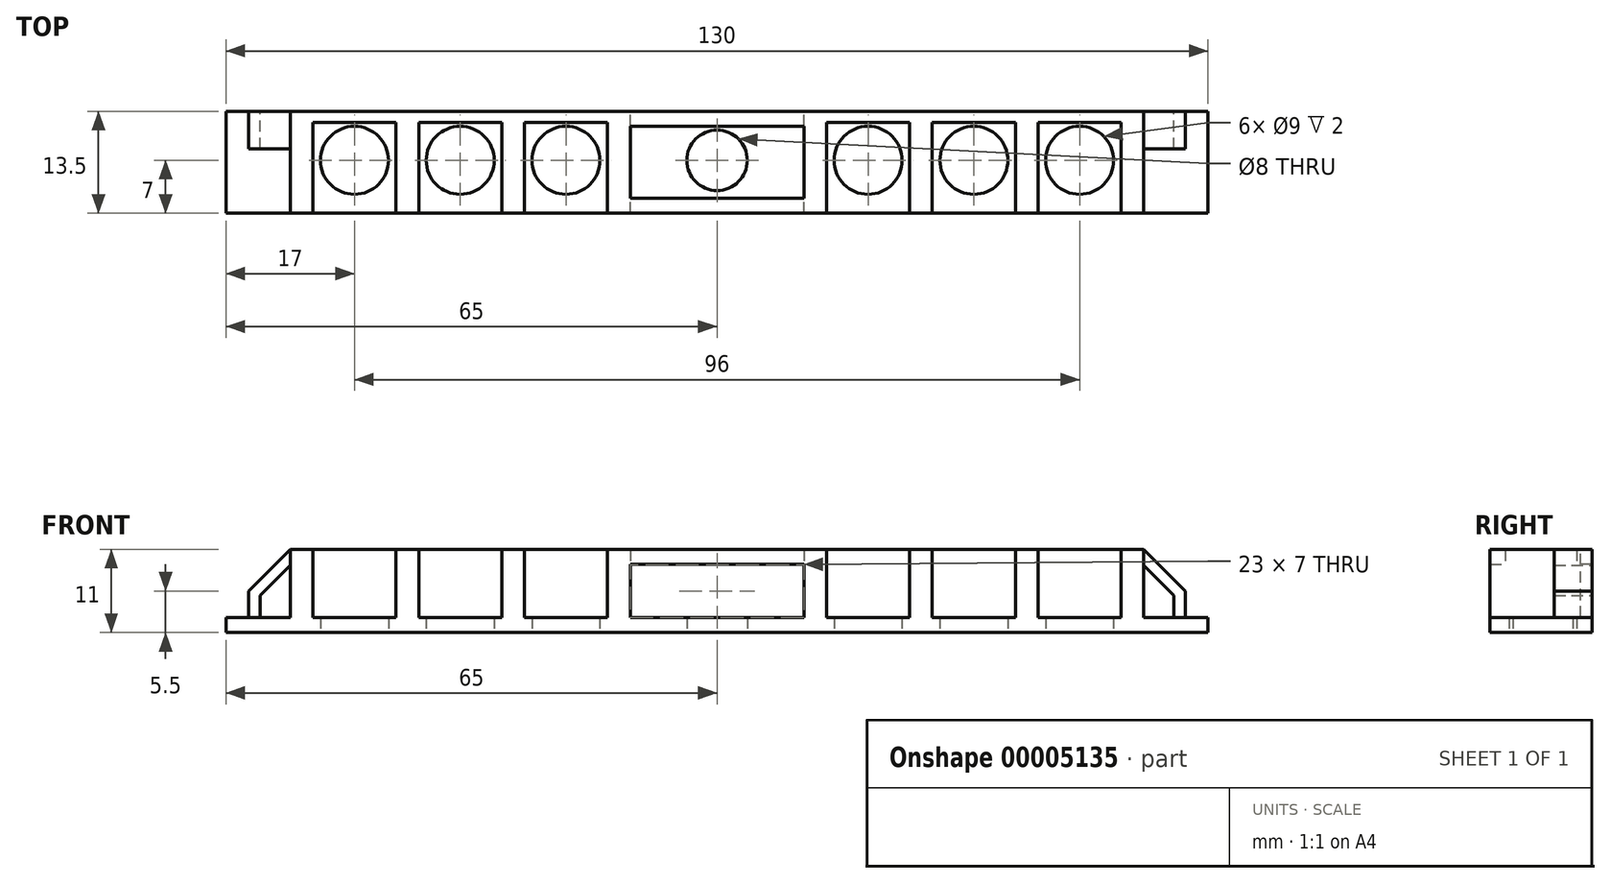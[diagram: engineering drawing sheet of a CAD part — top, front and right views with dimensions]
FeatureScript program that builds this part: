
annotation { "Feature Type Name" : "Feature", "Feature Type Description" : "" }
export const myFeature = defineFeature(function(context is Context, id is Id, definition is map)
    precondition{}
    {
        {
            var Q0;
            Q0=qCreatedBy(makeId("Top.planeOp"),FACE);
            var sketch = newSketch(context, id + "F0", { "sketchPlane" : qUnion([Q0])});
            skLineSegment(sketch, "E0", {"start": v(-20, 0) * mm, "end": v(-34, 0) * mm, "construction": true});
            skLineSegment(sketch, "E1", {"start": v(-34, 0) * mm, "end": v(-48, 0) * mm, "construction": true});
            skCircle(sketch, "E2", {"center": v(-20, 0) * mm, "radius": 4.5 * mm});
            skCircle(sketch, "E3", {"center": v(-34, 0) * mm, "radius": 4.5 * mm});
            skCircle(sketch, "E4", {"center": v(-48, 0) * mm, "radius": 4.5 * mm});
            skPoint(sketch, "E5", {"position": v(0, 0) * mm});
            skLineSegment(sketch, "E6.bottom", {"start": v(0, 6.5) * mm, "end": v(-65, 6.5) * mm});
            skLineSegment(sketch, "E6.top", {"start": v(0, -7) * mm, "end": v(-65, -7) * mm});
            skLineSegment(sketch, "E6.left", {"start": v(0, 6.5) * mm, "end": v(0, 4) * mm});
            skLineSegment(sketch, "E6.right", {"start": v(-65, 6.5) * mm, "end": v(-65, -7) * mm});
            skLineSegment(sketch, "E7", {"start": v(-20, 0) * mm, "end": v(-20, 6.5) * mm, "construction": true});
            skArc(sketch, "E8", {"start": v(0, 4) * mm, "mid": v(-4, 0) * mm, "end": v(0, -4) * mm});
            skLineSegment(sketch, "E9.trimOffspring", {"start": v(0, -4) * mm, "end": v(0, -7) * mm});
            skLineSegment(sketch, "E10", {"start": v(0, 4) * mm, "end": v(0, -4) * mm, "construction": true});
            skLineSegment(sketch, "E11", {"start": v(-20, 0) * mm, "end": v(0, 0) * mm, "construction": true});
            skSolve(sketch);
        }
        {
            var Q0;
            Q0 = qSketchRegion(id + "F0", true);
            extrude(context, id + "F1", {"entities" : qUnion([Q0]), "depth" : 2 * mm});
        }
        {
            var Q0;
            Q0=makeQuery(id+"F1.opExtrude","SWEPT_FACE",FACE,{"disambiguationData":[OSD([sQuery(id+"F0.wireOp",EDGE,"E6.bottom")])]});
            var sketch = newSketch(context, id + "F2", { "sketchPlane" : qUnion([Q0])});
            skLineSegment(sketch, "E12", {"start": v(20, 11) * mm, "end": v(20, 0) * mm, "construction": true});
            skLineSegment(sketch, "E13.bottom", {"start": v(11.5, 2) * mm, "end": v(14.5, 2) * mm});
            skLineSegment(sketch, "E13.top", {"start": v(11.5, 11) * mm, "end": v(14.5, 11) * mm});
            skLineSegment(sketch, "E13.left", {"start": v(11.5, 2) * mm, "end": v(11.5, 11) * mm});
            skLineSegment(sketch, "E13.right", {"start": v(14.5, 2) * mm, "end": v(14.5, 11) * mm});
            skLineSegment(sketch, "E14.bottom", {"start": v(25.5, 2) * mm, "end": v(28.5, 2) * mm});
            skLineSegment(sketch, "E14.top", {"start": v(25.5, 11) * mm, "end": v(28.5, 11) * mm});
            skLineSegment(sketch, "E14.left", {"start": v(25.5, 2) * mm, "end": v(25.5, 11) * mm});
            skLineSegment(sketch, "E14.right", {"start": v(28.5, 2) * mm, "end": v(28.5, 11) * mm});
            skLineSegment(sketch, "E15.bottom", {"start": v(39.5, 2) * mm, "end": v(42.5, 2) * mm});
            skLineSegment(sketch, "E15.top", {"start": v(39.5, 11) * mm, "end": v(42.5, 11) * mm});
            skLineSegment(sketch, "E15.left", {"start": v(39.5, 2) * mm, "end": v(39.5, 11) * mm});
            skLineSegment(sketch, "E15.right", {"start": v(42.5, 2) * mm, "end": v(42.5, 11) * mm});
            skLineSegment(sketch, "E16.bottom", {"start": v(53.5, 2) * mm, "end": v(56.5, 2) * mm});
            skLineSegment(sketch, "E16.top", {"start": v(53.5, 11) * mm, "end": v(56.5, 11) * mm});
            skLineSegment(sketch, "E16.left", {"start": v(53.5, 2) * mm, "end": v(53.5, 11) * mm});
            skLineSegment(sketch, "E16.right", {"start": v(56.5, 2) * mm, "end": v(56.5, 11) * mm});
            skLineSegment(sketch, "E17", {"start": v(14.5, 11) * mm, "end": v(25.5, 11) * mm, "construction": true});
            skLineSegment(sketch, "E18", {"start": v(28.5, 11) * mm, "end": v(39.5, 11) * mm, "construction": true});
            skLineSegment(sketch, "E19", {"start": v(42.5, 11) * mm, "end": v(53.5, 11) * mm, "construction": true});
            skLineSegment(sketch, "E20", {"start": v(48, 11) * mm, "end": v(48, 0) * mm, "construction": true});
            skSolve(sketch);
        }
        {
            var Q0;
            Q0 = qSketchRegion(id + "F2", true);
            extrude(context, id + "F3", {"entities" : qUnion([Q0]), "operationType" : NewBodyOperationType.ADD, "oppositeDirection" : true, "depth" : 13.5 * mm});
        }
        {
            var Q0;
            Q0=makeQuery(id+"F3.boolean.opBoolean","MERGE",FACE,{"derivedFrom":[makeQuery(id+"F1.opExtrude","SWEPT_FACE",FACE,{"disambiguationData":[OSD([sQuery(id+"F0.wireOp",EDGE,"E6.bottom")])]}),makeQuery(id+"F3.opExtrude","CAP_FACE",FACE,{"disambiguationData":[OSD([sQuery(id+"F2.wireOp",EDGE,"E13.bottom"),sQuery(id+"F2.wireOp",EDGE,"E13.top"),sQuery(id+"F2.wireOp",EDGE,"E13.left"),sQuery(id+"F2.wireOp",EDGE,"E13.right")])],"isStart":true}),makeQuery(id+"F3.opExtrude","CAP_FACE",FACE,{"disambiguationData":[OSD([sQuery(id+"F2.wireOp",EDGE,"E14.bottom"),sQuery(id+"F2.wireOp",EDGE,"E14.top"),sQuery(id+"F2.wireOp",EDGE,"E14.left"),sQuery(id+"F2.wireOp",EDGE,"E14.right")])],"isStart":true}),makeQuery(id+"F3.opExtrude","CAP_FACE",FACE,{"disambiguationData":[OSD([sQuery(id+"F2.wireOp",EDGE,"E15.bottom"),sQuery(id+"F2.wireOp",EDGE,"E15.top"),sQuery(id+"F2.wireOp",EDGE,"E15.left"),sQuery(id+"F2.wireOp",EDGE,"E15.right")])],"isStart":true}),makeQuery(id+"F3.opExtrude","CAP_FACE",FACE,{"disambiguationData":[OSD([sQuery(id+"F2.wireOp",EDGE,"E16.bottom"),sQuery(id+"F2.wireOp",EDGE,"E16.top"),sQuery(id+"F2.wireOp",EDGE,"E16.left"),sQuery(id+"F2.wireOp",EDGE,"E16.right")])],"isStart":true})]});
            var sketch = newSketch(context, id + "F4", { "sketchPlane" : qUnion([Q0])});
            skLineSegment(sketch, "E21.bottom", {"start": v(62, 2) * mm, "end": v(60.5, 2) * mm});
            skLineSegment(sketch, "E21.left", {"start": v(62, 2) * mm, "end": v(62, 5.5) * mm});
            skLineSegment(sketch, "E21.right", {"start": v(60.5, 2) * mm, "end": v(60.5, 4.88) * mm});
            skLineSegment(sketch, "E22", {"start": v(56.5, 11) * mm, "end": v(56.5, 8.88) * mm});
            skLineSegment(sketch, "E23", {"start": v(60.5, 4.88) * mm, "end": v(56.5, 8.88) * mm});
            skLineSegment(sketch, "E24", {"start": v(56.5, 11) * mm, "end": v(62, 5.5) * mm});
            skLineSegment(sketch, "E25", {"start": v(58.5, 6.88) * mm, "end": v(59.56, 7.94) * mm, "construction": true});
            skSolve(sketch);
        }
        {
            var Q0;
            Q0 = qSketchRegion(id + "F4", true);
            extrude(context, id + "F5", {"entities" : qUnion([Q0]), "operationType" : NewBodyOperationType.ADD, "oppositeDirection" : true, "depth" : 5 * mm});
        }
        {
            var Q0;
            Q0=makeQuery(id+"F1.opExtrude","SWEPT_FACE",FACE,{"disambiguationData":[OSD([sQuery(id+"F0.wireOp",EDGE,"E9.trimOffspring")])]});
            cPlane(context, id + "F6", {"entities" : qUnion([Q0]), "cplaneType" : CPlaneType.OFFSET, "offset" : 0 * mm, "width" : 150 * mm, "height" : 150 * mm});
        }
        {
            var Q0;
            Q0=makeQuery(id+"F1.opExtrude","SWEPT_BODY",BODY,{"disambiguationData":[OSD([sQuery(id+"F0.wireOp",EDGE,"E2"),sQuery(id+"F0.wireOp",EDGE,"E3"),sQuery(id+"F0.wireOp",EDGE,"E4"),sQuery(id+"F0.wireOp",EDGE,"E6.bottom"),sQuery(id+"F0.wireOp",EDGE,"E6.top"),sQuery(id+"F0.wireOp",EDGE,"E6.left"),sQuery(id+"F0.wireOp",EDGE,"E6.right"),sQuery(id+"F0.wireOp",EDGE,"E8"),sQuery(id+"F0.wireOp",EDGE,"E9.trimOffspring")])]});
            var Q1;
            Q1=qCreatedBy(id+"F6.planeOp",FACE);
            mirror(context, id + "F7", {"entities" : qUnion([Q0]), "mirrorPlane" : qUnion([Q1])});
        }
        {
            var Q0;
            Q0=makeQuery(id+"F1.opExtrude","SWEPT_BODY",BODY,{"disambiguationData":[OSD([sQuery(id+"F0.wireOp",EDGE,"E2"),sQuery(id+"F0.wireOp",EDGE,"E3"),sQuery(id+"F0.wireOp",EDGE,"E4"),sQuery(id+"F0.wireOp",EDGE,"E6.bottom"),sQuery(id+"F0.wireOp",EDGE,"E6.top"),sQuery(id+"F0.wireOp",EDGE,"E6.left"),sQuery(id+"F0.wireOp",EDGE,"E6.right"),sQuery(id+"F0.wireOp",EDGE,"E8"),sQuery(id+"F0.wireOp",EDGE,"E9.trimOffspring")])]});
            var Q1;
            Q1=makeQuery(id+"F7.opPattern","COPY",BODY,{"derivedFrom":makeQuery(id+"F1.opExtrude","SWEPT_BODY",BODY,{"disambiguationData":[OSD([sQuery(id+"F0.wireOp",EDGE,"E2"),sQuery(id+"F0.wireOp",EDGE,"E3"),sQuery(id+"F0.wireOp",EDGE,"E4"),sQuery(id+"F0.wireOp",EDGE,"E6.bottom"),sQuery(id+"F0.wireOp",EDGE,"E6.top"),sQuery(id+"F0.wireOp",EDGE,"E6.left"),sQuery(id+"F0.wireOp",EDGE,"E6.right"),sQuery(id+"F0.wireOp",EDGE,"E8"),sQuery(id+"F0.wireOp",EDGE,"E9.trimOffspring")])]}),"instanceName":"1"});
            booleanBodies(context, id + "F8", {"operationType" : BooleanOperationType.UNION, "tools" : qUnion([Q0, Q1])});
        }
        {
            var Q0;
            {var subQ0=makeQuery(id+"F1.opExtrude","CAP_FACE",FACE,{"disambiguationData":[OSD([sQuery(id+"F0.wireOp",EDGE,"E2"),sQuery(id+"F0.wireOp",EDGE,"E3"),sQuery(id+"F0.wireOp",EDGE,"E4"),sQuery(id+"F0.wireOp",EDGE,"E6.bottom"),sQuery(id+"F0.wireOp",EDGE,"E6.top"),sQuery(id+"F0.wireOp",EDGE,"E6.left"),sQuery(id+"F0.wireOp",EDGE,"E6.right"),sQuery(id+"F0.wireOp",EDGE,"E8"),sQuery(id+"F0.wireOp",EDGE,"E9.trimOffspring")])],"isStart":false});Q0=makeQuery(id+"F8.opBoolean","MERGE",FACE,{"derivedFrom":[subQ0,makeQuery(id+"F7.opPattern","COPY",FACE,{"derivedFrom":subQ0,"instanceName":"1"})]});}
            var sketch = newSketch(context, id + "F9", { "sketchPlane" : qUnion([Q0])});
            skLineSegment(sketch, "E26.bottom", {"start": v(-53.5, 6.5) * mm, "end": v(-14.5, 6.5) * mm});
            skLineSegment(sketch, "E26.top", {"start": v(-53.5, 5) * mm, "end": v(-14.5, 5) * mm});
            skLineSegment(sketch, "E26.left", {"start": v(-53.5, 6.5) * mm, "end": v(-53.5, 5) * mm});
            skLineSegment(sketch, "E26.right", {"start": v(-14.5, 6.5) * mm, "end": v(-14.5, 5) * mm});
            skLineSegment(sketch, "E27.bottom", {"start": v(14.5, 6.5) * mm, "end": v(53.5, 6.5) * mm});
            skLineSegment(sketch, "E27.top", {"start": v(14.5, 5) * mm, "end": v(53.5, 5) * mm});
            skLineSegment(sketch, "E27.left", {"start": v(14.5, 6.5) * mm, "end": v(14.5, 5) * mm});
            skLineSegment(sketch, "E27.right", {"start": v(53.5, 6.5) * mm, "end": v(53.5, 5) * mm});
            skSolve(sketch);
        }
        {
            var Q0;
            Q0 = qSketchRegion(id + "F9", true);
            var Q1;
            Q1=makeQuery(id+"F7.opPattern","COPY",FACE,{"derivedFrom":makeQuery(id+"F3.opExtrude","SWEPT_FACE",FACE,{"disambiguationData":[OSD([sQuery(id+"F2.wireOp",EDGE,"E16.top")])]}),"instanceName":"1"});
            extrude(context, id + "F10", {"entities" : qUnion([Q0]), "operationType" : NewBodyOperationType.ADD, "endBound" : BoundingType.UP_TO_SURFACE, "endBoundEntityFace" : qUnion([Q1]), "depth" : 25 * mm});
        }
        {
            var Q0;
            Q0=makeQuery(id+"F3.opExtrude","SWEPT_FACE",FACE,{"disambiguationData":[OSD([sQuery(id+"F2.wireOp",EDGE,"E13.left")])]});
            var sketch = newSketch(context, id + "F11", { "sketchPlane" : qUnion([Q0])});
            skLineSegment(sketch, "E28.bottom", {"start": v(-7, 11) * mm, "end": v(-5, 11) * mm});
            skLineSegment(sketch, "E28.top", {"start": v(-7, 9) * mm, "end": v(-5, 9) * mm});
            skLineSegment(sketch, "E28.left", {"start": v(-7, 11) * mm, "end": v(-7, 9) * mm});
            skLineSegment(sketch, "E28.right", {"start": v(-5, 11) * mm, "end": v(-5, 9) * mm});
            skLineSegment(sketch, "E29.bottom", {"start": v(6.5, 11) * mm, "end": v(4.5, 11) * mm});
            skLineSegment(sketch, "E29.top", {"start": v(6.5, 9) * mm, "end": v(4.5, 9) * mm});
            skLineSegment(sketch, "E29.left", {"start": v(6.5, 11) * mm, "end": v(6.5, 9) * mm});
            skLineSegment(sketch, "E29.right", {"start": v(4.5, 11) * mm, "end": v(4.5, 9) * mm});
            skSolve(sketch);
        }
        {
            var Q0;
            Q0 = qSketchRegion(id + "F11", true);
            extrude(context, id + "F12", {"entities" : qUnion([Q0]), "operationType" : NewBodyOperationType.ADD, "endBound" : BoundingType.UP_TO_NEXT, "depth" : 25 * mm});
        }
    });
